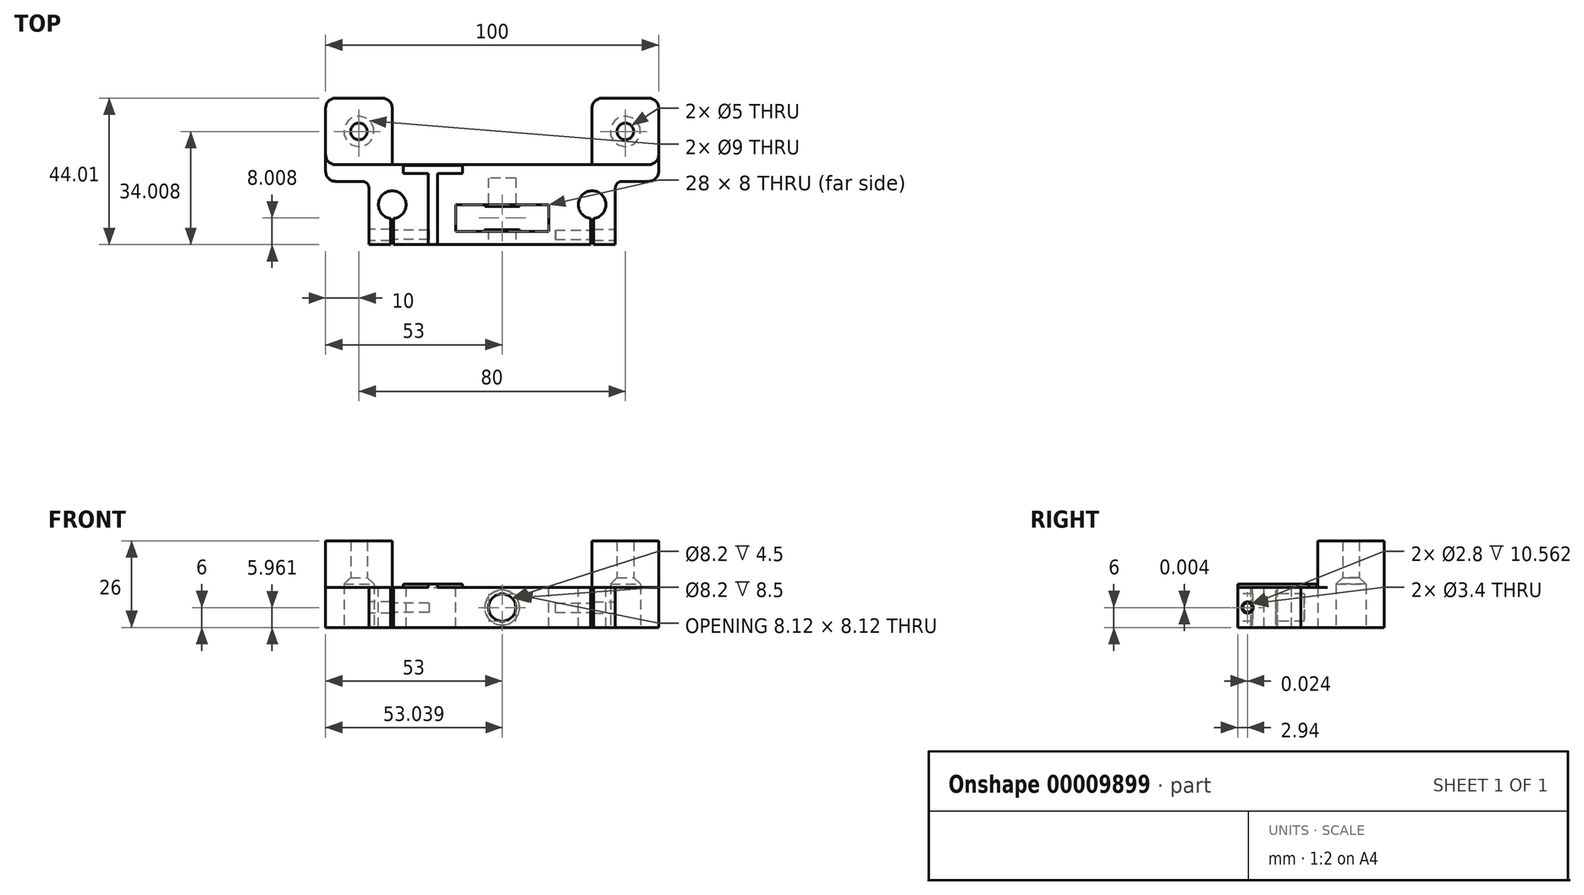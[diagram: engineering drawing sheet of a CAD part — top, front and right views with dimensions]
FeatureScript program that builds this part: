
annotation { "Feature Type Name" : "Feature", "Feature Type Description" : "" }
export const myFeature = defineFeature(function(context is Context, id is Id, definition is map)
    precondition{}
    {
        {
            var Q0;
            Q0=qCreatedBy(makeId("Top.planeOp"),FACE);
            var sketch = newSketch(context, id + "F0", { "sketchPlane" : qUnion([Q0])});
            skLineSegment(sketch, "E0", {"start": v(-46.35, 12.3) * mm, "end": v(53.65, 12.3) * mm});
            skLineSegment(sketch, "E1", {"start": v(53.65, 12.3) * mm, "end": v(53.65, 7.3) * mm});
            skLineSegment(sketch, "E2", {"start": v(53.65, 7.3) * mm, "end": v(40.65, 7.3) * mm});
            skLineSegment(sketch, "E3", {"start": v(40.65, 7.3) * mm, "end": v(40.65, -11.7) * mm});
            skLineSegment(sketch, "E4", {"start": v(40.65, -11.7) * mm, "end": v(-33.35, -11.7) * mm});
            skLineSegment(sketch, "E5", {"start": v(-33.35, -11.7) * mm, "end": v(-33.35, 7.3) * mm});
            skLineSegment(sketch, "E6", {"start": v(-33.35, 7.3) * mm, "end": v(-46.35, 7.3) * mm});
            skLineSegment(sketch, "E7", {"start": v(-46.35, 7.3) * mm, "end": v(-46.35, 12.3) * mm});
            skSolve(sketch);
        }
        {
            var Q0;
            Q0=qSketchRegion(id+"F0",true);
            extrude(context, id + "F1", {"entities" : qUnion([Q0]), "depth" : 12 * mm});
        }
        {
            var Q0;
            Q0=makeQuery(id+"F1.opExtrude","CAP_FACE",FACE,{"disambiguationData":[OSD([sQuery(id+"F0.wireOp",EDGE,"E0"),sQuery(id+"F0.wireOp",EDGE,"E1"),sQuery(id+"F0.wireOp",EDGE,"E2"),sQuery(id+"F0.wireOp",EDGE,"E3"),sQuery(id+"F0.wireOp",EDGE,"E4"),sQuery(id+"F0.wireOp",EDGE,"E5"),sQuery(id+"F0.wireOp",EDGE,"E6"),sQuery(id+"F0.wireOp",EDGE,"E7")])],"isStart":false});
            var sketch = newSketch(context, id + "F2", { "sketchPlane" : qUnion([Q0])});
            skCircle(sketch, "E8", {"center": v(-26.35, 0.3) * mm, "radius": 4.15 * mm});
            skCircle(sketch, "E9", {"center": v(33.65, 0.3) * mm, "radius": 4.15 * mm});
            skPoint(sketch, "E10", {"position": v(3.65, 12.3) * mm});
            skLineSegment(sketch, "E11.bottom", {"start": v(33.21, -3.01) * mm, "end": v(34.09, -3.01) * mm});
            skLineSegment(sketch, "E11.top", {"start": v(33.21, -12.27) * mm, "end": v(34.09, -12.27) * mm});
            skLineSegment(sketch, "E11.left", {"start": v(33.21, -3.01) * mm, "end": v(33.21, -12.27) * mm});
            skLineSegment(sketch, "E11.right", {"start": v(34.09, -3.01) * mm, "end": v(34.09, -12.27) * mm});
            skPoint(sketch, "E12", {"position": v(33.65, -3.01) * mm});
            skLineSegment(sketch, "E13", {"start": v(3.65, 12.3) * mm, "end": v(3.65, -11.7) * mm, "construction": true});
            skLineSegment(sketch, "E14.MirrorCS", {"start": v(-25.91, -12.27) * mm, "end": v(-26.79, -12.27) * mm});
            skLineSegment(sketch, "E15.MirrorCS", {"start": v(-26.79, -3.01) * mm, "end": v(-26.79, -12.27) * mm});
            skLineSegment(sketch, "E16.MirrorCS", {"start": v(-25.91, -3.01) * mm, "end": v(-26.79, -3.01) * mm});
            skLineSegment(sketch, "E17.MirrorCS", {"start": v(-25.91, -3.01) * mm, "end": v(-25.91, -12.27) * mm});
            skSolve(sketch);
        }
        {
            var Q0;
            Q0=qSketchRegion(id+"F2",true);
            var Q1;
            {var subQ3=sQuery(id+"F2.wireOp",EDGE,"E11.bottom");Q1=makeQuery(id+"F2.imprint","IMPRINT",FACE,{"disambiguationData":[TD([[makeQuery(id+"F2.imprint","IMPRINT",EDGE,{"derivedFrom":subQ3}),-1.0]])]});}
            var Q2;
            {var subQ3=sQuery(id+"F2.wireOp",EDGE,"E16.MirrorCS");Q2=makeQuery(id+"F2.imprint","IMPRINT",FACE,{"disambiguationData":[TD([[makeQuery(id+"F2.imprint","IMPRINT",EDGE,{"derivedFrom":subQ3}),1.0]])]});}
            extrude(context, id + "F3", {"entities" : qUnion([Q0, Q1, Q2]), "operationType" : NewBodyOperationType.REMOVE, "endBound" : BoundingType.THROUGH_ALL, "oppositeDirection" : true, "depth" : 25 * mm});
        }
        {
            var Q0;
            Q0=makeQuery(id+"F1.opExtrude","SWEPT_FACE",FACE,{"disambiguationData":[OSD([sQuery(id+"F0.wireOp",EDGE,"E4")])]});
            var sketch = newSketch(context, id + "F4", { "sketchPlane" : qUnion([Q0])});
            skLineSegment(sketch, "E18", {"start": v(-33.35, 6) * mm, "end": v(40.65, 6) * mm, "construction": true});
            skCircle(sketch, "E19", {"center": v(6.65, 6) * mm, "radius": 4.1 * mm});
            skSolve(sketch);
        }
        {
            var Q0;
            Q0=qSketchRegion(id+"F4",true);
            extrude(context, id + "F5", {"entities" : qUnion([Q0]), "operationType" : NewBodyOperationType.REMOVE, "oppositeDirection" : true, "depth" : 20 * mm});
        }
        {
            var Q0;
            Q0=makeQuery(id+"F1.opExtrude","CAP_FACE",FACE,{"disambiguationData":[OSD([sQuery(id+"F0.wireOp",EDGE,"E0"),sQuery(id+"F0.wireOp",EDGE,"E1"),sQuery(id+"F0.wireOp",EDGE,"E2"),sQuery(id+"F0.wireOp",EDGE,"E3"),sQuery(id+"F0.wireOp",EDGE,"E4"),sQuery(id+"F0.wireOp",EDGE,"E5"),sQuery(id+"F0.wireOp",EDGE,"E6"),sQuery(id+"F0.wireOp",EDGE,"E7")])],"isStart":false});
            var sketch = newSketch(context, id + "F6", { "sketchPlane" : qUnion([Q0])});
            skLineSegment(sketch, "E20.bottom", {"start": v(-7.35, 0.3) * mm, "end": v(20.65, 0.3) * mm});
            skLineSegment(sketch, "E20.top", {"start": v(-7.35, -7.7) * mm, "end": v(20.65, -7.7) * mm});
            skLineSegment(sketch, "E20.left", {"start": v(-7.35, 0.3) * mm, "end": v(-7.35, -7.7) * mm});
            skLineSegment(sketch, "E20.right", {"start": v(20.65, 0.3) * mm, "end": v(20.65, -7.7) * mm});
            skLineSegment(sketch, "E21", {"start": v(6.65, 12.3) * mm, "end": v(6.65, -11.7) * mm, "construction": true});
            skLineSegment(sketch, "E22", {"start": v(6.65, 0.3) * mm, "end": v(6.65, -7.7) * mm});
            skSolve(sketch);
        }
        {
            var Q0;
            Q0=qSketchRegion(id+"F6",true);
            extrude(context, id + "F7", {"entities" : qUnion([Q0]), "operationType" : NewBodyOperationType.REMOVE, "endBound" : BoundingType.THROUGH_ALL, "oppositeDirection" : true, "depth" : 25 * mm});
        }
        {
            var Q0;
            Q0=makeQuery(id+"F7.boolean.opBoolean","COPY",FACE,{"derivedFrom":makeQuery(id+"F7.opExtrude","SWEPT_FACE",FACE,{"disambiguationData":[OSD([sQuery(id+"F6.wireOp",EDGE,"E20.bottom")])]})});
            var sketch = newSketch(context, id + "F8", { "sketchPlane" : qUnion([Q0])});
            skCircle(sketch, "E23", {"center": v(6.65, 6) * mm, "radius": 5.2 * mm});
            skSolve(sketch);
        }
        {
            var Q0;
            Q0=makeQuery(id+"F8.imprint","IMPRINT",FACE,{"disambiguationData":[TD([[makeQuery(id+"F8.imprint","IMPRINT",EDGE,{"derivedFrom":sQuery(id+"F8.wireOp",EDGE,"E23")}),1.0]])]});
            extrude(context, id + "F9", {"entities" : qUnion([Q0]), "operationType" : NewBodyOperationType.ADD, "depth" : 0.5 * mm});
        }
        {
            var Q0;
            Q0=makeQuery(id+"F7.boolean.opBoolean","COPY",FACE,{"derivedFrom":makeQuery(id+"F7.opExtrude","SWEPT_FACE",FACE,{"disambiguationData":[OSD([sQuery(id+"F6.wireOp",EDGE,"E20.top")])]})});
            var sketch = newSketch(context, id + "F10", { "sketchPlane" : qUnion([Q0])});
            skCircle(sketch, "E24", {"center": v(-6.65, 6) * mm, "radius": 5.25 * mm});
            skSolve(sketch);
        }
        {
            var Q0;
            Q0=makeQuery(id+"F10.imprint","IMPRINT",FACE,{"disambiguationData":[TD([[makeQuery(id+"F10.imprint","IMPRINT",EDGE,{"derivedFrom":sQuery(id+"F10.wireOp",EDGE,"E24")}),1.0]])]});
            extrude(context, id + "F11", {"entities" : qUnion([Q0]), "operationType" : NewBodyOperationType.ADD, "depth" : 0.5 * mm});
        }
        {
            var Q0;
            Q0=makeQuery(id+"F1.opExtrude","CAP_FACE",FACE,{"disambiguationData":[OSD([sQuery(id+"F0.wireOp",EDGE,"E0"),sQuery(id+"F0.wireOp",EDGE,"E1"),sQuery(id+"F0.wireOp",EDGE,"E2"),sQuery(id+"F0.wireOp",EDGE,"E3"),sQuery(id+"F0.wireOp",EDGE,"E4"),sQuery(id+"F0.wireOp",EDGE,"E5"),sQuery(id+"F0.wireOp",EDGE,"E6"),sQuery(id+"F0.wireOp",EDGE,"E7")])],"isStart":false});
            var sketch = newSketch(context, id + "F12", { "sketchPlane" : qUnion([Q0])});
            skText(sketch, "E25", { "text": "T", "fontName": "OpenSans-Regular.ttf"});
            const initialGuessF12  = {"E25": [-0.02337, -0.0117, 1, 0, 0.024]};
            skSetInitialGuess(sketch, initialGuessF12);
            skSolve(sketch);
        }
        {
            var Q0;
            Q0=qSketchRegion(id+"F12",true);
            extrude(context, id + "F13", {"entities" : qUnion([Q0]), "operationType" : NewBodyOperationType.ADD, "depth" : 1 * mm});
        }
        {
            var Q0;
            Q0=makeQuery(id+"F1.opExtrude","SWEPT_FACE",FACE,{"disambiguationData":[OSD([sQuery(id+"F0.wireOp",EDGE,"E3")])]});
            var sketch = newSketch(context, id + "F14", { "sketchPlane" : qUnion([Q0])});
            skCircle(sketch, "E26", {"center": v(-8.74, 6) * mm, "radius": 1.7 * mm});
            skCircle(sketch, "E27", {"center": v(-8.74, 6) * mm, "radius": 1.4 * mm});
            skLineSegment(sketch, "E28", {"start": v(-11.7, 6) * mm, "end": v(-3.84, 6) * mm, "construction": true});
            skSolve(sketch);
        }
        {
            var Q0;
            Q0=makeQuery(id+"F14.imprint","IMPRINT",FACE,{"disambiguationData":[TD([[makeQuery(id+"F14.imprint","IMPRINT",EDGE,{"derivedFrom":sQuery(id+"F14.wireOp",EDGE,"E27")}),1.0]])]});
            extrude(context, id + "F15", {"entities" : qUnion([Q0]), "operationType" : NewBodyOperationType.REMOVE, "oppositeDirection" : true, "depth" : 18 * mm});
        }
        {
            var Q0;
            Q0=makeQuery(id+"F14.imprint","IMPRINT",FACE,{"disambiguationData":[TD([[makeQuery(id+"F14.imprint","IMPRINT",EDGE,{"derivedFrom":sQuery(id+"F14.wireOp",EDGE,"E27")}),1.0]])]});
            var Q1;
            Q1=makeQuery(id+"F14.imprint","IMPRINT",FACE,{"disambiguationData":[TD([[makeQuery(id+"F14.imprint","IMPRINT",EDGE,{"derivedFrom":sQuery(id+"F14.wireOp",EDGE,"E26")}),1.0]])]});
            extrude(context, id + "F16", {"entities" : qUnion([Q0, Q1]), "operationType" : NewBodyOperationType.REMOVE, "endBound" : BoundingType.UP_TO_NEXT, "oppositeDirection" : true, "depth" : 7 * mm});
        }
        {
            var Q0;
            Q0=makeQuery(id+"F1.opExtrude","SWEPT_EDGE",EDGE,{"disambiguationData":[OSD([sQuery(id+"F0.wireOp",EDGE,"E2"),sQuery(id+"F0.wireOp",EDGE,"E3")])]});
            fillet(context, id + "F17", {"entities" : qUnion([Q0]), "radius" : 2 * mm, "tangentPropagation" : true, "allowEdgeOverflow" : false});
        }
        {
            var Q0;
            Q0=makeQuery(id+"F1.opExtrude","SWEPT_FACE",FACE,{"disambiguationData":[OSD([sQuery(id+"F0.wireOp",EDGE,"E5")])]});
            var sketch = newSketch(context, id + "F18", { "sketchPlane" : qUnion([Q0])});
            skCircle(sketch, "E29", {"center": v(8.76, 6) * mm, "radius": 1.7 * mm});
            skCircle(sketch, "E30", {"center": v(8.76, 6) * mm, "radius": 1.4 * mm});
            skLineSegment(sketch, "E31", {"start": v(8.76, 0) * mm, "end": v(8.76, 12) * mm, "construction": true});
            skSolve(sketch);
        }
        {
            var Q0;
            Q0=makeQuery(id+"F18.imprint","IMPRINT",FACE,{"disambiguationData":[TD([[makeQuery(id+"F18.imprint","IMPRINT",EDGE,{"derivedFrom":sQuery(id+"F18.wireOp",EDGE,"E30")}),1.0]])]});
            extrude(context, id + "F19", {"entities" : qUnion([Q0]), "operationType" : NewBodyOperationType.REMOVE, "oppositeDirection" : true, "depth" : 18 * mm});
        }
        {
            var Q0;
            Q0=makeQuery(id+"F18.imprint","IMPRINT",FACE,{"disambiguationData":[TD([[makeQuery(id+"F18.imprint","IMPRINT",EDGE,{"derivedFrom":sQuery(id+"F18.wireOp",EDGE,"E30")}),1.0]])]});
            var Q1;
            Q1=makeQuery(id+"F18.imprint","IMPRINT",FACE,{"disambiguationData":[TD([[makeQuery(id+"F18.imprint","IMPRINT",EDGE,{"derivedFrom":sQuery(id+"F18.wireOp",EDGE,"E29")}),1.0]])]});
            extrude(context, id + "F20", {"entities" : qUnion([Q0, Q1]), "operationType" : NewBodyOperationType.REMOVE, "endBound" : BoundingType.UP_TO_NEXT, "oppositeDirection" : true, "depth" : 25 * mm});
        }
        {
            var Q0;
            Q0=makeQuery(id+"F1.opExtrude","SWEPT_EDGE",EDGE,{"disambiguationData":[OSD([sQuery(id+"F0.wireOp",EDGE,"E5"),sQuery(id+"F0.wireOp",EDGE,"E6")])]});
            fillet(context, id + "F21", {"entities" : qUnion([Q0]), "radius" : 2 * mm, "tangentPropagation" : true, "allowEdgeOverflow" : false});
        }
        {
            var Q0;
            Q0=makeQuery(id+"F1.opExtrude","SWEPT_FACE",FACE,{"disambiguationData":[OSD([sQuery(id+"F0.wireOp",EDGE,"E0")])]});
            var sketch = newSketch(context, id + "F22", { "sketchPlane" : qUnion([Q0])});
            skLineSegment(sketch, "E32.bottom", {"start": v(-53.65, 12) * mm, "end": v(-33.65, 12) * mm});
            skLineSegment(sketch, "E32.top", {"start": v(-53.65, 0) * mm, "end": v(-33.65, 0) * mm});
            skLineSegment(sketch, "E32.left", {"start": v(-53.65, 12) * mm, "end": v(-53.65, 0) * mm});
            skLineSegment(sketch, "E32.right", {"start": v(-33.65, 12) * mm, "end": v(-33.65, 0) * mm});
            skLineSegment(sketch, "E33.bottom", {"start": v(46.35, 12) * mm, "end": v(26.35, 12) * mm});
            skLineSegment(sketch, "E33.top", {"start": v(46.35, 0) * mm, "end": v(26.35, 0) * mm});
            skLineSegment(sketch, "E33.left", {"start": v(46.35, 12) * mm, "end": v(46.35, 0) * mm});
            skLineSegment(sketch, "E33.right", {"start": v(26.35, 12) * mm, "end": v(26.35, 0) * mm});
            skSolve(sketch);
        }
        {
            var Q0;
            Q0 = qSketchRegion(id + "F22", true);
            extrude(context, id + "F23", {"entities" : qUnion([Q0]), "operationType" : NewBodyOperationType.ADD, "depth" : 20 * mm});
        }
        {
            var Q0;
            Q0=makeQuery(id+"F23.boolean.opBoolean","MERGE",FACE,{"derivedFrom":[makeQuery(id+"F1.opExtrude","CAP_FACE",FACE,{"disambiguationData":[OSD([sQuery(id+"F0.wireOp",EDGE,"E0"),sQuery(id+"F0.wireOp",EDGE,"E1"),sQuery(id+"F0.wireOp",EDGE,"E2"),sQuery(id+"F0.wireOp",EDGE,"E3"),sQuery(id+"F0.wireOp",EDGE,"E4"),sQuery(id+"F0.wireOp",EDGE,"E5"),sQuery(id+"F0.wireOp",EDGE,"E6"),sQuery(id+"F0.wireOp",EDGE,"E7")])],"isStart":false}),makeQuery(id+"F23.opExtrude","SWEPT_FACE",FACE,{"disambiguationData":[OSD([sQuery(id+"F22.wireOp",EDGE,"E32.bottom")])]}),makeQuery(id+"F23.opExtrude","SWEPT_FACE",FACE,{"disambiguationData":[OSD([sQuery(id+"F22.wireOp",EDGE,"E33.bottom")])]})]});
            var sketch = newSketch(context, id + "F24", { "sketchPlane" : qUnion([Q0])});
            skLineSegment(sketch, "E34.bottom", {"start": v(-46.35, 32.3) * mm, "end": v(-26.35, 32.3) * mm});
            skLineSegment(sketch, "E34.top", {"start": v(-46.35, 12.3) * mm, "end": v(-26.35, 12.3) * mm});
            skLineSegment(sketch, "E34.left", {"start": v(-46.35, 32.3) * mm, "end": v(-46.35, 12.3) * mm});
            skLineSegment(sketch, "E34.right", {"start": v(-26.35, 32.3) * mm, "end": v(-26.35, 12.3) * mm});
            skLineSegment(sketch, "E35.bottom", {"start": v(53.65, 32.3) * mm, "end": v(33.65, 32.3) * mm});
            skLineSegment(sketch, "E35.top", {"start": v(53.65, 12.3) * mm, "end": v(33.65, 12.3) * mm});
            skLineSegment(sketch, "E35.left", {"start": v(53.65, 32.3) * mm, "end": v(53.65, 12.3) * mm});
            skLineSegment(sketch, "E35.right", {"start": v(33.65, 32.3) * mm, "end": v(33.65, 12.3) * mm});
            skSolve(sketch);
        }
        {
            var Q0;
            Q0 = qSketchRegion(id + "F24", true);
            extrude(context, id + "F25", {"entities" : qUnion([Q0]), "operationType" : NewBodyOperationType.ADD, "depth" : 14 * mm});
        }
        {
            var Q0;
            Q0=makeQuery(id+"F23.boolean.opBoolean","MERGE",FACE,{"derivedFrom":[makeQuery(id+"F1.opExtrude","CAP_FACE",FACE,{"disambiguationData":[OSD([sQuery(id+"F0.wireOp",EDGE,"E0"),sQuery(id+"F0.wireOp",EDGE,"E1"),sQuery(id+"F0.wireOp",EDGE,"E2"),sQuery(id+"F0.wireOp",EDGE,"E3"),sQuery(id+"F0.wireOp",EDGE,"E4"),sQuery(id+"F0.wireOp",EDGE,"E5"),sQuery(id+"F0.wireOp",EDGE,"E6"),sQuery(id+"F0.wireOp",EDGE,"E7")])],"isStart":true}),makeQuery(id+"F23.opExtrude","SWEPT_FACE",FACE,{"disambiguationData":[OSD([sQuery(id+"F22.wireOp",EDGE,"E32.top")])]}),makeQuery(id+"F23.opExtrude","SWEPT_FACE",FACE,{"disambiguationData":[OSD([sQuery(id+"F22.wireOp",EDGE,"E33.top")])]})]});
            var sketch = newSketch(context, id + "F26", { "sketchPlane" : qUnion([Q0])});
            skCircle(sketch, "E36", {"center": v(-36.35, -22.3) * mm, "radius": 2.5 * mm});
            skCircle(sketch, "E37", {"center": v(43.65, -22.3) * mm, "radius": 2.5 * mm});
            skPoint(sketch, "E38", {"position": v(-36.35, -32.3) * mm});
            skPoint(sketch, "E39", {"position": v(43.65, -32.3) * mm});
            skCircle(sketch, "E40", {"center": v(-36.35, -22.3) * mm, "radius": 4.5 * mm});
            skCircle(sketch, "E41", {"center": v(43.65, -22.3) * mm, "radius": 4.5 * mm});
            skSolve(sketch);
        }
        {
            var Q0;
            Q0=makeQuery(id+"F26.imprint","IMPRINT",FACE,{"disambiguationData":[TD([[makeQuery(id+"F26.imprint","IMPRINT",EDGE,{"derivedFrom":sQuery(id+"F26.wireOp",EDGE,"E36")}),1.0]])]});
            var Q1;
            Q1=makeQuery(id+"F26.imprint","IMPRINT",FACE,{"disambiguationData":[TD([[makeQuery(id+"F26.imprint","IMPRINT",EDGE,{"derivedFrom":sQuery(id+"F26.wireOp",EDGE,"E37")}),1.0]])]});
            extrude(context, id + "F27", {"entities" : qUnion([Q0, Q1]), "operationType" : NewBodyOperationType.REMOVE, "endBound" : BoundingType.THROUGH_ALL, "oppositeDirection" : true, "depth" : 25 * mm});
        }
        {
            var Q0;
            Q0=makeQuery(id+"F1.opExtrude","SWEPT_EDGE",EDGE,{"disambiguationData":[OSD([sQuery(id+"F0.wireOp",EDGE,"E6"),sQuery(id+"F0.wireOp",EDGE,"E7")])]});
            var Q1;
            Q1=makeQuery(id+"F23.opExtrude","CAP_EDGE",EDGE,{"disambiguationData":[OSD([sQuery(id+"F22.wireOp",EDGE,"E33.left")])],"isStart":false});
            var Q2;
            Q2=makeQuery(id+"F23.opExtrude","CAP_EDGE",EDGE,{"disambiguationData":[OSD([sQuery(id+"F22.wireOp",EDGE,"E33.right")])],"isStart":false});
            var Q3;
            Q3=makeQuery(id+"F23.opExtrude","CAP_EDGE",EDGE,{"disambiguationData":[OSD([sQuery(id+"F22.wireOp",EDGE,"E33.right")])],"isStart":true});
            var Q4;
            Q4=makeQuery(id+"F23.opExtrude","CAP_EDGE",EDGE,{"disambiguationData":[OSD([sQuery(id+"F22.wireOp",EDGE,"E32.right")])],"isStart":true});
            var Q5;
            Q5=makeQuery(id+"F23.opExtrude","CAP_EDGE",EDGE,{"disambiguationData":[OSD([sQuery(id+"F22.wireOp",EDGE,"E32.right")])],"isStart":false});
            var Q6;
            Q6=makeQuery(id+"F23.opExtrude","CAP_EDGE",EDGE,{"disambiguationData":[OSD([sQuery(id+"F22.wireOp",EDGE,"E32.left")])],"isStart":false});
            var Q7;
            Q7=makeQuery(id+"F1.opExtrude","SWEPT_EDGE",EDGE,{"disambiguationData":[OSD([sQuery(id+"F0.wireOp",EDGE,"E1"),sQuery(id+"F0.wireOp",EDGE,"E2")])]});
            var Q8;
            Q8=makeQuery(id+"F25.opExtrude","SWEPT_EDGE",EDGE,{"disambiguationData":[OSD([sQuery(id+"F0.wireOp",EDGE,"E7"),sQuery(id+"F22.wireOp",EDGE,"E33.bottom"),sQuery(id+"F22.wireOp",EDGE,"E33.left"),sQuery(id+"F24.wireOp",EDGE,"E34.top"),sQuery(id+"F24.wireOp",EDGE,"E34.left")])]});
            var Q9;
            Q9=makeQuery(id+"F25.opExtrude","SWEPT_EDGE",EDGE,{"disambiguationData":[OSD([sQuery(id+"F0.wireOp",EDGE,"E1"),sQuery(id+"F22.wireOp",EDGE,"E32.bottom"),sQuery(id+"F22.wireOp",EDGE,"E32.left"),sQuery(id+"F24.wireOp",EDGE,"E35.top"),sQuery(id+"F24.wireOp",EDGE,"E35.left")])]});
            fillet(context, id + "F28", {"entities" : qUnion([Q0, Q1, Q2, Q3, Q4, Q5, Q6, Q7, Q8, Q9]), "radius" : 3 * mm, "tangentPropagation" : true, "allowEdgeOverflow" : false});
        }
        {
            var Q0;
            Q0=makeQuery(id+"F26.imprint","IMPRINT",FACE,{"disambiguationData":[TD([[makeQuery(id+"F26.imprint","IMPRINT",EDGE,{"derivedFrom":sQuery(id+"F26.wireOp",EDGE,"E36")}),-1.0]])]});
            var Q1;
            Q1=makeQuery(id+"F26.imprint","IMPRINT",FACE,{"disambiguationData":[TD([[makeQuery(id+"F26.imprint","IMPRINT",EDGE,{"derivedFrom":sQuery(id+"F26.wireOp",EDGE,"E37")}),-1.0]])]});
            extrude(context, id + "F29", {"entities" : qUnion([Q0, Q1]), "operationType" : NewBodyOperationType.REMOVE, "oppositeDirection" : true, "depth" : 16 * mm});
        }
        {
            var Q0;
            Q0=makeQuery(id+"F29.boolean.opBoolean","COPY",EDGE,{"derivedFrom":makeQuery(id+"F29.opExtrude","CAP_EDGE",EDGE,{"disambiguationData":[OSD([sQuery(id+"F26.wireOp",EDGE,"E40")])],"isStart":false})});
            var Q1;
            Q1=makeQuery(id+"F29.boolean.opBoolean","COPY",EDGE,{"derivedFrom":makeQuery(id+"F29.opExtrude","CAP_EDGE",EDGE,{"disambiguationData":[OSD([sQuery(id+"F26.wireOp",EDGE,"E41")])],"isStart":false})});
            chamfer(context, id + "F30", {"entities" : qUnion([Q0, Q1]), "width" : 3 * mm, "tangentPropagation" : true});
        }
    });
